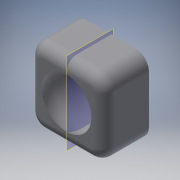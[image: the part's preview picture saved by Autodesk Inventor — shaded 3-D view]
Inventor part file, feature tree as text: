
AUTODESK INVENTOR PART (.ipt)
format: ipt  version: 2016 (Build 200138000, 138)  size: 158,208 bytes
history: native  units: in
note: dims shown in document units (in); Inventor stores cm internally (conversion verified against a paired STEP export)
features: sketch x3, extrude x2, fillet x2, reference x2, plane x1, revolve x1
ambient origin geometry x8: Origin, YZ Plane, XZ Plane, XY Plane, X Axis, Y Axis, Z Axis, Center Point
bodies: Solid1 (feature_tree)
feature tree (11):
  extrude  "Extrusion1"  Depth=0.0787in
  plane  "Work Plane1"
  revolve  "Revolution1"  [1 undecoded]
  extrude  "Extrusion3"  [1 undecoded]
  fillet  "Fillet1"  [1 undecoded]
  fillet  "Fillet2"  Radius=0.268in
  sketch  "Sketch1"  dims[d0=0.0787in d1=0.0787in]
  reference  "Reference1"
  sketch  "Sketch2"  dims[d2=0.0787in d3=0.0787in]
  reference  "Reference2"
  sketch  "Sketch4"  dims[d4=0.4134in d5=0.0in d6=-0.3465in d7=90.0deg d10=0.268in d11=0.0in d12=0.125in d13=0.1in]
note: 3 required parameter values undecoded (feature->parameter linkage not recoverable at this tier; creation-order binding heuristic only, values carry confidence <= 0.55)